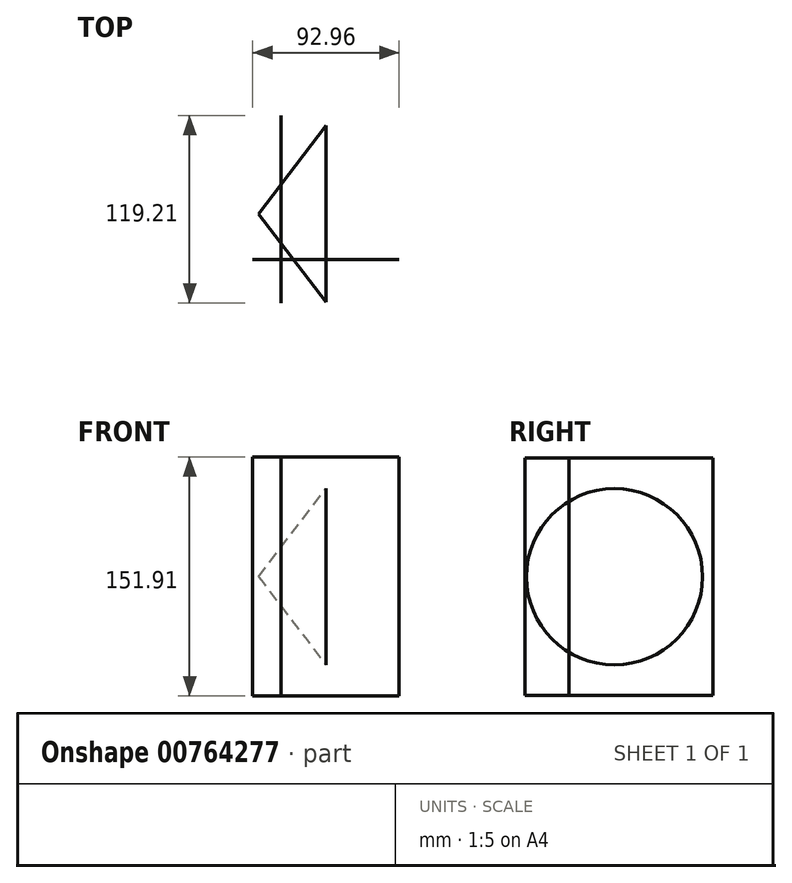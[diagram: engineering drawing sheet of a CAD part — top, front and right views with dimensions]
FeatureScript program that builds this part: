
annotation { "Feature Type Name" : "Feature", "Feature Type Description" : "" }
export const myFeature = defineFeature(function(context is Context, id is Id, definition is map)
    precondition{}
    {
        {
            var Q0;
            Q0=qCreatedBy(makeId("Front.planeOp"),FACE);
            var sketch = newSketch(context, id + "F0", { "sketchPlane" : qUnion([Q0])});
            skLineSegment(sketch, "E0", {"start": v(0, 55.95) * mm, "end": v(-42.86, 0) * mm});
            skLineSegment(sketch, "E1", {"start": v(-42.86, 0) * mm, "end": v(0, 0) * mm});
            skLineSegment(sketch, "E2", {"start": v(0, 0) * mm, "end": v(0, 55.95) * mm});
            skSolve(sketch);
        }
        {
            var Q0;
            Q0=makeQuery(id+"F0.imprint","IMPRINT",FACE,{"disambiguationData":[TD([[makeQuery(id+"F0.imprint","IMPRINT",EDGE,{"derivedFrom":sQuery(id+"F0.wireOp",EDGE,"E0")}),1.0]])]});
            var Q1;
            Q1=sQuery(id+"F0.wireOp",EDGE,"E0");
            var Q2;
            Q2=sQuery(id+"F0.wireOp",EDGE,"E1");
            revolve(context, id + "F1", {"bodyType" : ToolBodyType.SURFACE, "surfaceOperationType" : NewSurfaceOperationType.NEW, "entities" : qUnion([Q0]), "surfaceEntities" : qUnion([Q1]), "axis" : qUnion([Q2]), "revolveType" : RevolveType.FULL});
        }
        {
            var Q0;
            Q0=qCreatedBy(makeId("Right.planeOp"),FACE);
            var sketch = newSketch(context, id + "F2", { "sketchPlane" : qUnion([Q0])});
            skLineSegment(sketch, "E3", {"start": v(-28.85, 76.23) * mm, "end": v(-28.85, -75.68) * mm});
            skSolve(sketch);
        }
        {
            var Q0;
            Q0=sQuery(id+"F2.wireOp",EDGE,"E3");
            extrude(context, id + "F3", {"bodyType" : ToolBodyType.SURFACE, "surfaceEntities" : qUnion([Q0]), "endBound" : BoundingType.SYMMETRIC, "oppositeDirection" : true, "depth" : 92.96 * mm, "offsetDistance" : 25.4 * mm});
        }
        {
            var Q0;
            Q0=qCreatedBy(makeId("Top.planeOp"),FACE);
            var sketch = newSketch(context, id + "F4", { "sketchPlane" : qUnion([Q0])});
            skLineSegment(sketch, "E4", {"start": v(-28.57, -56.76) * mm, "end": v(-28.57, 62.45) * mm});
            skSolve(sketch);
        }
        {
            var Q0;
            Q0=sQuery(id+"F4.wireOp",EDGE,"E4");
            extrude(context, id + "F5", {"bodyType" : ToolBodyType.SURFACE, "surfaceEntities" : qUnion([Q0]), "endBound" : BoundingType.SYMMETRIC, "depth" : 150.88 * mm, "offsetDistance" : 25.4 * mm});
        }
    });
